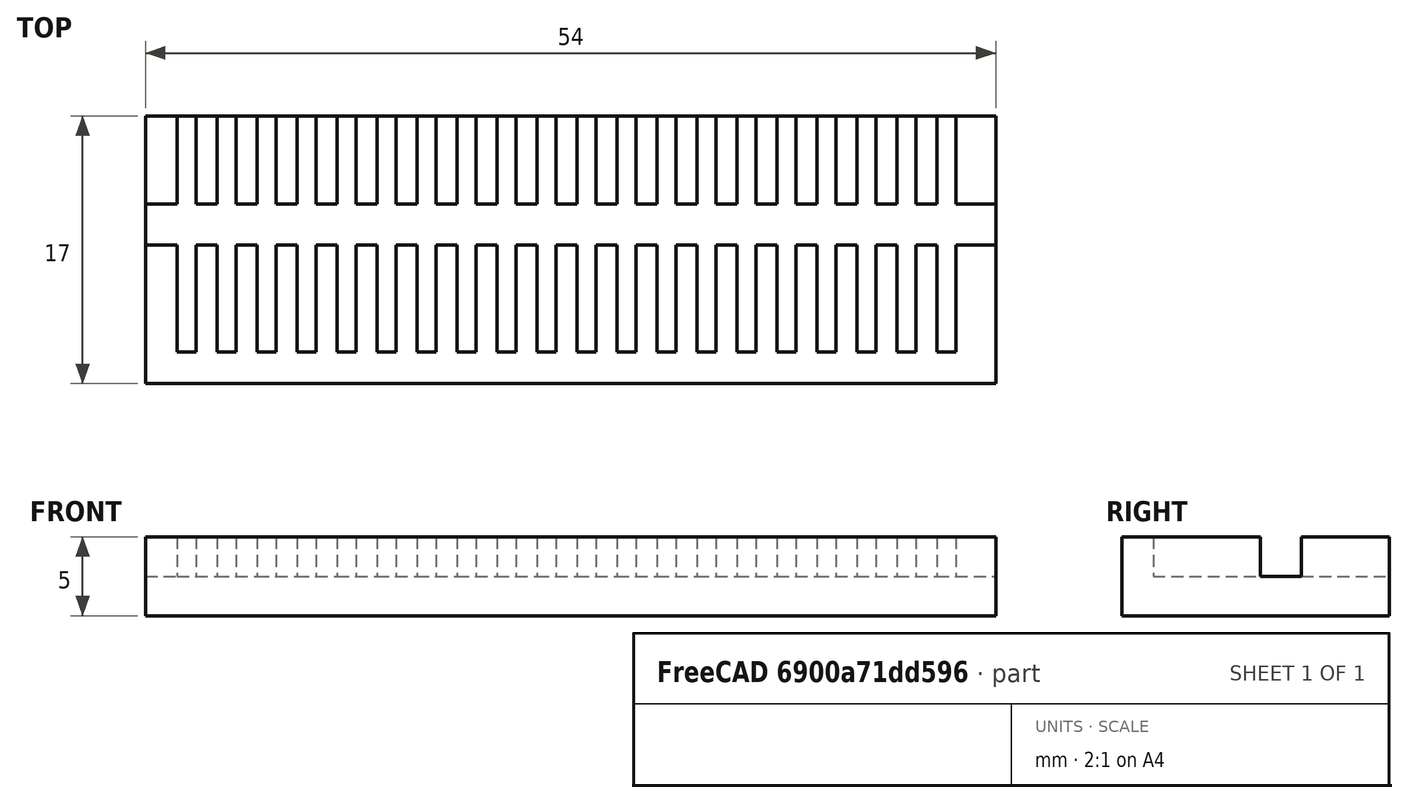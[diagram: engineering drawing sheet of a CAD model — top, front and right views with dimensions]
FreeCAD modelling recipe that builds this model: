
FCSTD DOCUMENT  (FreeCAD 0.18R4 (GitTag))
Label: molde
License: All rights reserved
LicenseURL: http://en.wikipedia.org/wiki/All_rights_reserved
objects: Part::Box×4, Part::Cut×2, Part::FeaturePython×1, Part::MultiFuse×1, Mesh::Feature×1
note: 8 computed .brp shape members not serialized (recipe doc carries the construction recipe); baked Part::Feature solids carry a one-line shape summary decoded from their .brp

FEATURE [Part::Box] Box  label="Cube"
  AttacherType = Attacher::AttachEngine3D
  Height = 5
  Length = 54
  Width = 15
FEATURE [Part::Box] Box001  label="Cube001"
  AttacherType = Attacher::AttachEngine3D
  Height = 8
  Length = 1.2
  Placement = pos=(2,-4,2.5) rot=(0,0,1;0rad)
  Width = 20
FEATURE [Part::FeaturePython] Array  # Draft array (typed FeaturePython)
  Angle = 360
  ArrayType = 0
  Axis = (0,0,1)
  Base = -> Box001
  Center = (0,0,0)
  Fuse = false
  IntervalAxis = (0,0,0)
  IntervalX = (2.54,0,0)
  IntervalY = (0,1,0)
  IntervalZ = (0,0,1)
  NumberPolar = 1
  NumberX = 20
  NumberY = 1
  NumberZ = 1
FEATURE [Part::Cut] Cut
  Base = -> Box
  Refine = true
  Tool = -> Array
FEATURE [Part::Box] Box002  label="Cube002"
  AttacherType = Attacher::AttachEngine3D
  Height = 2.6
  Length = 56
  Placement = pos=(-1,6.8,2.5) rot=(0,0,1;0rad)
  Width = 2.6
FEATURE [Part::Box] Box003  label="Cube003"
  AttacherType = Attacher::AttachEngine3D
  Height = 5
  Length = 54
  Placement = pos=(0,-2,0) rot=(0,0,1;0rad)
  Width = 2
FEATURE [Part::MultiFuse] Fusion
  Refine = true
  Shapes = -> [Cut,Box003]
FEATURE [Part::Cut] Cut001
  Base = -> Fusion
  Refine = true
  Tool = -> Box002
FEATURE [Mesh::Feature] Mesh  label="Cut001 (Meshed)"
